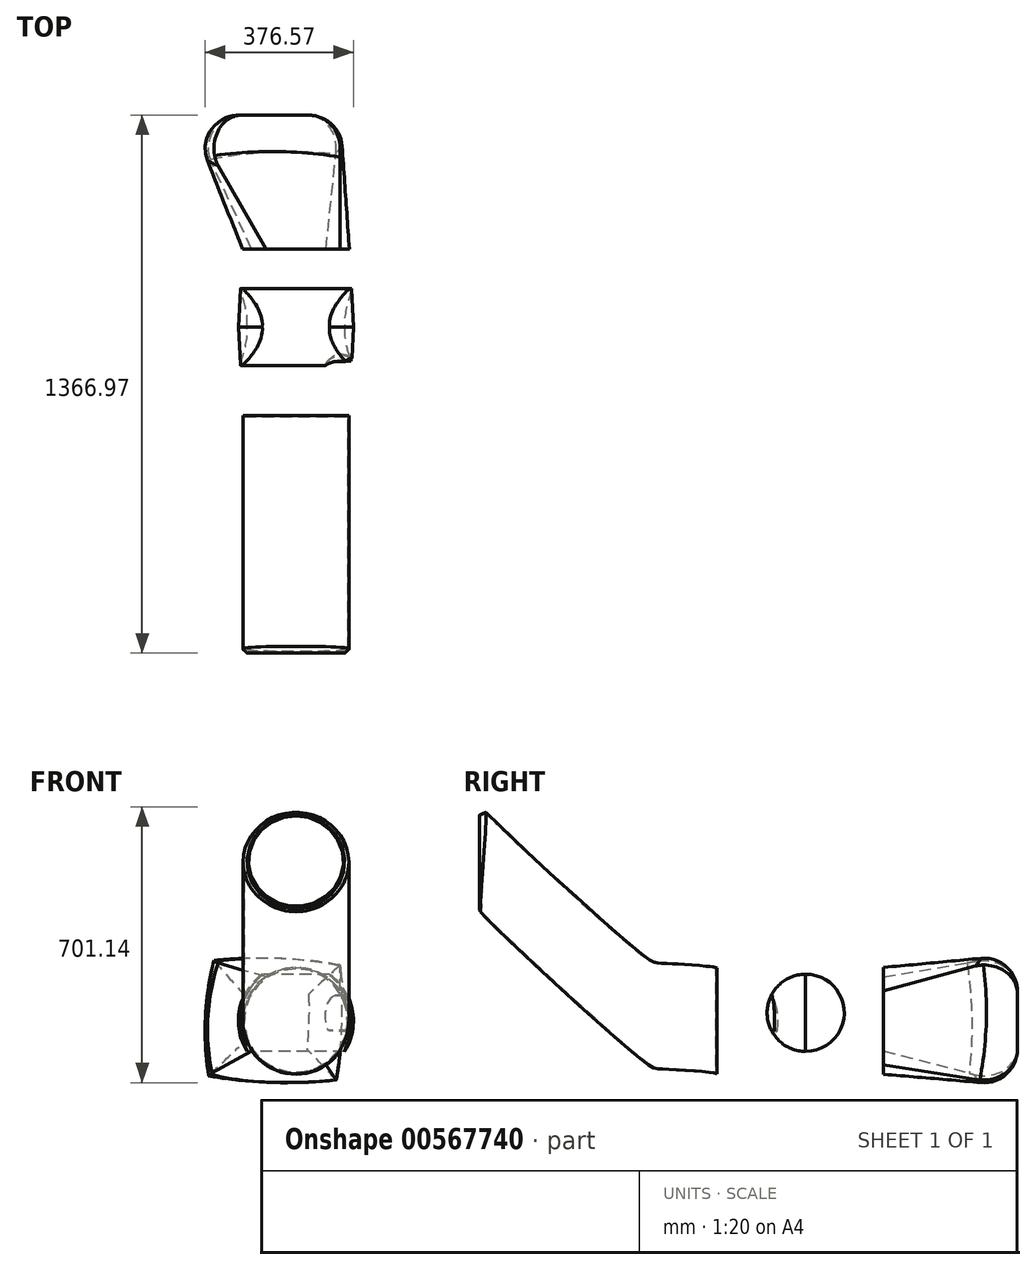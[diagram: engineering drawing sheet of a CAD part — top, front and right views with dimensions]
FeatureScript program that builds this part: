
annotation { "Feature Type Name" : "Feature", "Feature Type Description" : "" }
export const myFeature = defineFeature(function(context is Context, id is Id, definition is map)
    precondition{}
    {
        {
            var Q0;
            Q0=qCreatedBy(makeId("Front.planeOp"),FACE);
            var sketch = newSketch(context, id + "F0", { "sketchPlane" : qUnion([Q0])});
            skCircle(sketch, "E0", {"center": v(0, 0) * mm, "radius": 146.1 * mm});
            skSolve(sketch);
        }
        {
            var Q0;
            Q0 = qSketchRegion(id + "F0", true);
            extrude(context, id + "F1", {"entities" : qUnion([Q0]), "depth" : 225 * mm, "offsetDistance" : 25 * mm, "hasDraft" : true, "draftAngle" : 3 * degree, "draftPullDirection" : true, "hasSecondDirection" : true, "secondDirectionOppositeDirection" : true, "secondDirectionDepth" : 198 * mm, "hasSecondDirectionDraft" : true, "secondDirectionDraftAngle" : 3 * degree, "secondDirectionDraftPullDirection" : true});
        }
        {
            var Q0;
            Q0=makeQuery(id+"F1.opExtrude","CAP_FACE",FACE,{"disambiguationData":[OSD([sQuery(id+"F0.wireOp",EDGE,"E0")])],"isStart":false});
            var sketch = newSketch(context, id + "F2", { "sketchPlane" : qUnion([Q0])});
            skLineSegment(sketch, "E1", {"start": v(-17.05, 0) * mm, "end": v(217.62, 0) * mm, "construction": true});
            skCircle(sketch, "E2", {"center": v(115.28, 109.72) * mm, "radius": 44.93 * mm});
            skSolve(sketch);
        }
        {
            var Q0;
            {var subQ0=sQuery(id+"F2.wireOp",EDGE,"E2");var subQ1=makeQuery(id+"F1.opExtrude","CAP_EDGE",EDGE,{"disambiguationData":[OSD([sQuery(id+"F0.wireOp",EDGE,"E0")])],"isStart":false});var subQ2=makeQuery(id+"F2.imprint","INTERSECT",VERTEX,{"disambiguationData":[OD(0.0)],"derivedFrom":[subQ1,subQ0]});Q0=makeQuery(id+"F2.imprint","IMPRINT",FACE,{"disambiguationData":[TD([[makeQuery(id+"F2.imprint","IMPRINT",EDGE,{"disambiguationData":[TD([[subQ2,1.0]])],"derivedFrom":subQ0}),1.0]])]});}
            var Q1;
            Q1=sQuery(id+"F2.wireOp",EDGE,"E2");
            var Q2;
            Q2=sQuery(id+"F2.wireOp",EDGE,"E1");
            revolve(context, id + "F3", {"operationType" : NewBodyOperationType.REMOVE, "entities" : qUnion([Q0]), "surfaceEntities" : qUnion([Q1]), "axis" : qUnion([Q2]), "revolveType" : RevolveType.TWO_DIRECTIONS, "angle" : 295 * degree, "angleBack" : 260 * degree});
        }
        {
            var Q0;
            Q0=qCreatedBy(makeId("Right.planeOp"),FACE);
            var sketch = newSketch(context, id + "F4", { "sketchPlane" : qUnion([Q0])});
            skFitSpline(sketch, "E3", {"points": [v(-225, 121.94) * mm, v(-270.5, 128.31) * mm, v(-365.66, 133.93) * mm, v(-411.74, 153.41) * mm, v(-828.97, 536.68) * mm], "startDerivative": vector(-95.06, 45.64) * mm, "endDerivative": vector(-110.53, 161.1) * mm});
            skSolve(sketch);
        }
        {
            var Q0;
            Q0=makeQuery(id+"F1.opExtrude","CAP_FACE",FACE,{"disambiguationData":[OSD([sQuery(id+"F0.wireOp",EDGE,"E0")])],"isStart":false});
            var Q1;
            Q1=sQuery(id+"F4.wireOp",EDGE,"E3");
            sweep(context, id + "F5", {"profiles" : qUnion([Q0]), "path" : qUnion([Q1]), "keepProfileOrientation" : true});
        }
        {
            var Q0;
            Q0=makeQuery(id+"F1.opExtrude","CAP_FACE",FACE,{"disambiguationData":[OSD([sQuery(id+"F0.wireOp",EDGE,"E0")])],"isStart":true});
            cPlane(context, id + "F6", {"entities" : qUnion([Q0]), "cplaneType" : CPlaneType.OFFSET, "offset" : 340 * mm, "width" : 150 * mm, "height" : 150 * mm});
        }
        {
            var Q0;
            Q0=qCreatedBy(id+"F6.planeOp",FACE);
            var sketch = newSketch(context, id + "F7", { "sketchPlane" : qUnion([Q0])});
            skLineSegment(sketch, "E4.bottom", {"start": v(-111.92, -164.54) * mm, "end": v(270.47, -164.54) * mm});
            skLineSegment(sketch, "E4.top", {"start": v(-111.92, 167.64) * mm, "end": v(270.47, 167.64) * mm});
            skLineSegment(sketch, "E4.left", {"start": v(-111.92, -164.54) * mm, "end": v(-111.92, 167.64) * mm});
            skLineSegment(sketch, "E4.right", {"start": v(270.47, -164.54) * mm, "end": v(270.47, 167.64) * mm});
            skSolve(sketch);
        }
        {
            var Q0;
            Q0=makeQuery(id+"F1.opExtrude","CAP_FACE",FACE,{"disambiguationData":[OSD([sQuery(id+"F0.wireOp",EDGE,"E0")])],"isStart":true});
            var Q1;
            Q1=makeQuery(id+"F7.imprint","IMPRINT",FACE,{"disambiguationData":[TD([[makeQuery(id+"F7.imprint","IMPRINT",EDGE,{"derivedFrom":sQuery(id+"F7.wireOp",EDGE,"E4.bottom")}),1.0]])]});
            loft(context, id + "F8", {"sheetProfilesArray" : [{ "sheetProfileEntities" : qUnion([Q0]) }, { "sheetProfileEntities" : qUnion([Q1]) }]});
        }
        {
            var Q0;
            Q0=makeQuery(id+"F8.opLoft","MID_CAP_EDGE",EDGE,{"disambiguationData":[OSD([sQuery(id+"F7.wireOp",EDGE,"E4.bottom"),sQuery(id+"F7.wireOp",EDGE,"E4.top"),sQuery(id+"F7.wireOp",EDGE,"E4.right")])],"capPos":1.0});
            var Q1;
            Q1=makeQuery(id+"F8.opLoft","MID_CAP_EDGE",EDGE,{"disambiguationData":[OSD([sQuery(id+"F7.wireOp",EDGE,"E4.top"),sQuery(id+"F7.wireOp",EDGE,"E4.left"),sQuery(id+"F7.wireOp",EDGE,"E4.right")])],"capPos":1.0});
            var Q2;
            Q2=makeQuery(id+"F8.opLoft","MID_CAP_EDGE",EDGE,{"disambiguationData":[OSD([sQuery(id+"F7.wireOp",EDGE,"E4.bottom"),sQuery(id+"F7.wireOp",EDGE,"E4.top"),sQuery(id+"F7.wireOp",EDGE,"E4.left")])],"capPos":1.0});
            var Q3;
            Q3=makeQuery(id+"F8.opLoft","MID_CAP_EDGE",EDGE,{"disambiguationData":[OSD([sQuery(id+"F7.wireOp",EDGE,"E4.bottom"),sQuery(id+"F7.wireOp",EDGE,"E4.left"),sQuery(id+"F7.wireOp",EDGE,"E4.right")])],"capPos":1.0});
            fillet(context, id + "F9", {"entities" : qUnion([Q0, Q1, Q2, Q3]), "radius" : 84.78 * mm, "tangentPropagation" : true, "allowEdgeOverflow" : false});
        }
        {
            var Q0;
            Q0=makeQuery(id+"F5.opSweep","CAP_EDGE",EDGE,{"disambiguationData":[OSD([sQuery(id+"F0.wireOp",EDGE,"E0"),sQuery(id+"F4.wireOp",VERTEX,"E3.end")])],"isStart":false});
            chamfer(context, id + "F10", {"entities" : qUnion([Q0]), "width" : 10 * mm});
        }
        {
            var Q0;
            Q0=makeQuery(id+"F5.opSweep","CAP_FACE",FACE,{"disambiguationData":[OSD([sQuery(id+"F0.wireOp",EDGE,"E0"),sQuery(id+"F4.wireOp",VERTEX,"E3.end")])],"isStart":false});
            shell(context, id + "F11", {"entities" : qUnion([Q0]), "thickness" : 2.5 * mm});
        }
        {
            var Q0;
            Q0=qCreatedBy(makeId("Right.planeOp"),FACE);
            var sketch = newSketch(context, id + "F12", { "sketchPlane" : qUnion([Q0])});
            skCircle(sketch, "E5", {"center": v(0, 20.45) * mm, "radius": 98.02 * mm});
            skSolve(sketch);
        }
        {
            var Q0;
            Q0 = qSketchRegion(id + "F12", true);
            extrude(context, id + "F13", {"entities" : qUnion([Q0]), "endBound" : BoundingType.SYMMETRIC, "depth" : 438 * mm, "offsetDistance" : 25 * mm});
        }
        {
            var Q0;
            Q0=makeQuery(id+"F13.opExtrude","SWEPT_BODY",BODY,{"disambiguationData":[OSD([sQuery(id+"F12.wireOp",EDGE,"E5")])]});
            var Q1;
            Q1=makeQuery(id+"F1.*.split.splitOp","SPLIT",BODY,{"derivedFrom":makeQuery(id+"F1.opExtrude","SWEPT_BODY",BODY,{"disambiguationData":[OSD([sQuery(id+"F0.wireOp",EDGE,"E0")])]})});
            var Q2;
            Q2=makeQuery(id+"F8.opLoft","SWEPT_BODY",BODY,{"disambiguationData":[OSD([sQuery(id+"F0.wireOp",EDGE,"E0"),makeQuery(id+"F7.imprint","IMPRINT",FACE,{"disambiguationData":[TD([[makeQuery(id+"F7.imprint","IMPRINT",EDGE,{"derivedFrom":sQuery(id+"F7.wireOp",EDGE,"E4.bottom")}),1.0]])]})])]});
            booleanBodies(context, id + "F14", {"operationType" : BooleanOperationType.INTERSECTION, "tools" : qUnion([Q0, Q1]), "targets" : qUnion([Q2])});
        }
    });
